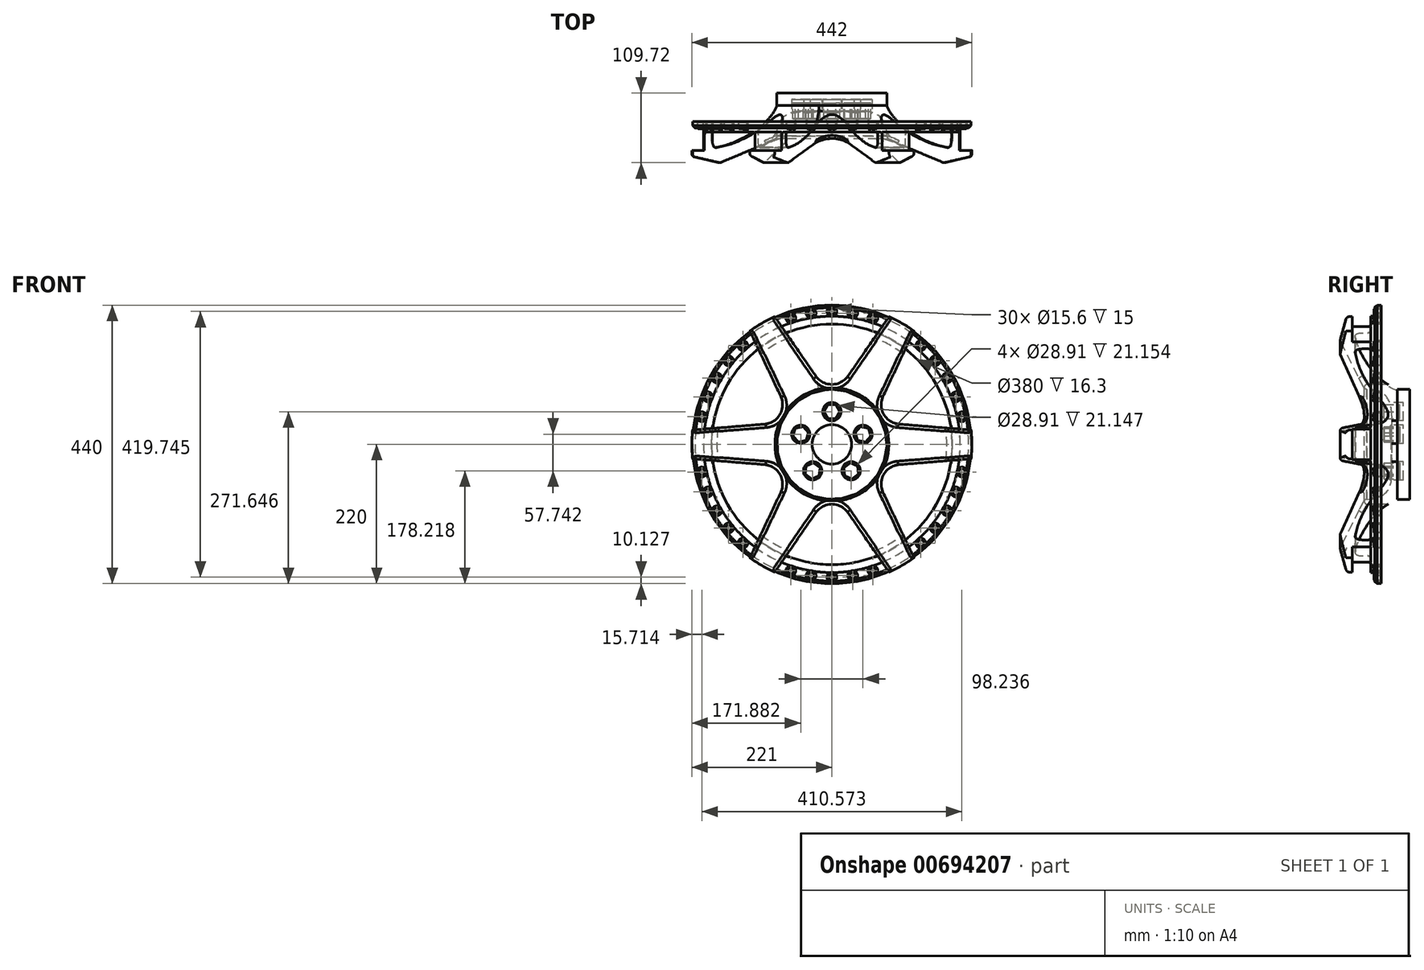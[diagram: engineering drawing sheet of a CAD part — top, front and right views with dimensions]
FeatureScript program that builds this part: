
annotation { "Feature Type Name" : "Feature", "Feature Type Description" : "" }
export const myFeature = defineFeature(function(context is Context, id is Id, definition is map)
    precondition{}
    {
        {
            var Q0;
            Q0=qCreatedBy(makeId("Front.planeOp"),FACE);
            var sketch = newSketch(context, id + "F0", { "sketchPlane" : qUnion([Q0])});
            skLineSegment(sketch, "E0", {"start": v(-376.44, 221) * mm, "end": v(379.77, 221) * mm, "construction": true});
            skLineSegment(sketch, "E1", {"start": v(-377.46, 0) * mm, "end": v(367.57, 0) * mm, "construction": true});
            skLineSegment(sketch, "E2", {"start": v(0, 375.13) * mm, "end": v(0, -409.58) * mm, "construction": true});
            skLineSegment(sketch, "E3", {"start": v(-369.36, 188.3) * mm, "end": v(384.11, 188.3) * mm, "construction": true});
            skLineSegment(sketch, "E4", {"start": v(-370.28, 96.42) * mm, "end": v(351.95, 96.42) * mm, "construction": true});
            skSolve(sketch);
        }
        {
            var Q0;
            Q0=qCreatedBy(makeId("Right.planeOp"),FACE);
            var sketch = newSketch(context, id + "F1", { "sketchPlane" : qUnion([Q0])});
            skLineSegment(sketch, "E5", {"start": v(-189.06, 0) * mm, "end": v(214.1, 0) * mm, "construction": true});
            skLineSegment(sketch, "E6", {"start": v(-201.77, 221) * mm, "end": v(212.06, 221) * mm, "construction": true});
            skLineSegment(sketch, "E7", {"start": v(-20.76, 221) * mm, "end": v(-30.79, 177.87) * mm});
            skLineSegment(sketch, "E8", {"start": v(8.3, 86.81) * mm, "end": v(8.3, 0) * mm});
            skLineSegment(sketch, "E9", {"start": v(8.3, 0) * mm, "end": v(79.17, 0) * mm});
            skLineSegment(sketch, "E10", {"start": v(79.17, 0) * mm, "end": v(79.17, 86.81) * mm});
            skLineSegment(sketch, "E11", {"start": v(79.17, 86.81) * mm, "end": v(59.77, 86.81) * mm});
            skFitSpline(sketch, "E12", {"points": [v(59.77, 86.81) * mm, v(-6.25, 181.47) * mm], "startDerivative": vector(-82.57, 26.6) * mm, "endDerivative": vector(-18.74, 115.71) * mm});
            skLineSegment(sketch, "E13", {"start": v(-20.76, 221) * mm, "end": v(-11.33, 221) * mm});
            skLineSegment(sketch, "E14", {"start": v(-11.33, 221) * mm, "end": v(-11.33, 202.63) * mm});
            skLineSegment(sketch, "E15", {"start": v(-11.33, 202.63) * mm, "end": v(19.19, 202.63) * mm});
            skLineSegment(sketch, "E16", {"start": v(19.19, 202.63) * mm, "end": v(19.19, 190.64) * mm});
            skFitSpline(sketch, "E17", {"points": [v(19.19, 190.64) * mm, v(-6.25, 181.47) * mm], "startDerivative": vector(-49.6, -1.13) * mm, "endDerivative": vector(9.02, -31.56) * mm});
            skLineSegment(sketch, "E18", {"start": v(-30.79, 177.87) * mm, "end": v(8.3, 86.81) * mm});
            skSolve(sketch);
        }
        {
            var Q0;
            Q0 = qSketchRegion(id + "F1", true);
            var Q1;
            Q1=sQuery(id+"F1.wireOp",EDGE,"E5");
            revolve(context, id + "F2", {"entities" : qUnion([Q0]), "axis" : qUnion([Q1]), "revolveType" : RevolveType.FULL});
        }
        {
            var Q0;
            Q0=qCreatedBy(makeId("Front.planeOp"),FACE);
            var sketch = newSketch(context, id + "F3", { "sketchPlane" : qUnion([Q0])});
            skLineSegment(sketch, "E19", {"start": v(0, 306.65) * mm, "end": v(0, -154.44) * mm, "construction": true});
            skLineSegment(sketch, "E20", {"start": v(-91.12, 202.94) * mm, "end": v(-25.47, 108.01) * mm});
            skLineSegment(sketch, "E21.MirrorCS", {"start": v(91.12, 202.94) * mm, "end": v(25.47, 108.01) * mm});
            skArc(sketch, "E22", {"start": v(-91.12, 202.94) * mm, "mid": v(0, 222.46) * mm, "end": v(91.12, 202.94) * mm});
            skArc(sketch, "E23", {"start": v(-25.47, 108.01) * mm, "mid": v(0, 94.66) * mm, "end": v(25.47, 108.01) * mm});
            skLineSegment(sketch, "E24.1.0", {"start": v(-130.2, 180.39) * mm, "end": v(-80.8, 76.06) * mm});
            skArc(sketch, "E24.1.1", {"start": v(-106.28, 31.95) * mm, "mid": v(-81.98, 47.33) * mm, "end": v(-80.8, 76.06) * mm});
            skLineSegment(sketch, "E24.1.2", {"start": v(-221.32, 22.56) * mm, "end": v(-106.28, 31.95) * mm});
            skArc(sketch, "E24.1.3", {"start": v(-221.32, 22.56) * mm, "mid": v(-192.66, 111.23) * mm, "end": v(-130.2, 180.39) * mm});
            skLineSegment(sketch, "E24.2.0", {"start": v(-221.32, -22.56) * mm, "end": v(-106.28, -31.95) * mm});
            skArc(sketch, "E24.2.1", {"start": v(-80.8, -76.06) * mm, "mid": v(-81.98, -47.33) * mm, "end": v(-106.28, -31.95) * mm});
            skLineSegment(sketch, "E24.2.2", {"start": v(-130.2, -180.39) * mm, "end": v(-80.8, -76.06) * mm});
            skArc(sketch, "E24.2.3", {"start": v(-130.2, -180.39) * mm, "mid": v(-192.66, -111.23) * mm, "end": v(-221.32, -22.56) * mm});
            skLineSegment(sketch, "E24.3.0", {"start": v(-91.12, -202.94) * mm, "end": v(-25.47, -108.01) * mm});
            skArc(sketch, "E24.3.1", {"start": v(25.47, -108.01) * mm, "mid": v(0, -94.66) * mm, "end": v(-25.47, -108.01) * mm});
            skLineSegment(sketch, "E24.3.2", {"start": v(91.12, -202.94) * mm, "end": v(25.47, -108.01) * mm});
            skArc(sketch, "E24.3.3", {"start": v(91.12, -202.94) * mm, "mid": v(0, -222.46) * mm, "end": v(-91.12, -202.94) * mm});
            skLineSegment(sketch, "E24.4.0", {"start": v(130.2, -180.39) * mm, "end": v(80.8, -76.06) * mm});
            skArc(sketch, "E24.4.1", {"start": v(106.28, -31.95) * mm, "mid": v(81.98, -47.33) * mm, "end": v(80.8, -76.06) * mm});
            skLineSegment(sketch, "E24.4.2", {"start": v(221.32, -22.56) * mm, "end": v(106.28, -31.95) * mm});
            skArc(sketch, "E24.4.3", {"start": v(221.32, -22.56) * mm, "mid": v(192.66, -111.23) * mm, "end": v(130.2, -180.39) * mm});
            skLineSegment(sketch, "E24.5.0", {"start": v(221.32, 22.56) * mm, "end": v(106.28, 31.95) * mm});
            skArc(sketch, "E24.5.1", {"start": v(80.8, 76.06) * mm, "mid": v(81.98, 47.33) * mm, "end": v(106.28, 31.95) * mm});
            skLineSegment(sketch, "E24.5.2", {"start": v(130.2, 180.39) * mm, "end": v(80.8, 76.06) * mm});
            skArc(sketch, "E24.5.3", {"start": v(130.2, 180.39) * mm, "mid": v(192.66, 111.23) * mm, "end": v(221.32, 22.56) * mm});
            skSolve(sketch);
        }
        {
            var Q0;
            Q0 = qSketchRegion(id + "F3", true);
            extrude(context, id + "F4", {"entities" : qUnion([Q0]), "operationType" : NewBodyOperationType.REMOVE, "oppositeDirection" : true, "depth" : 214 * mm, "offsetDistance" : 25 * mm, "symmetric" : true});
        }
        {
            var Q0;
            Q0=qCreatedBy(makeId("Front.planeOp"),FACE);
            var sketch = newSketch(context, id + "F5", { "sketchPlane" : qUnion([Q0])});
            skCircle(sketch, "E25.0", {"center": v(0, 0) * mm, "radius": 86.81 * mm});
            skSolve(sketch);
        }
        {
            var Q0;
            Q0 = qSketchRegion(id + "F5", true);
            extrude(context, id + "F6", {"entities" : qUnion([Q0]), "operationType" : NewBodyOperationType.REMOVE, "oppositeDirection" : true, "depth" : 51 * mm, "offsetDistance" : 25 * mm});
        }
        {
            var Q0;
            Q0=makeQuery(id+"F6.boolean.opBoolean","COPY",EDGE,{"derivedFrom":makeQuery(id+"F6.opExtrude","CAP_EDGE",EDGE,{"disambiguationData":[OSD([sQuery(id+"F5.wireOp",EDGE,"E25.0")])],"isStart":false})});
            fillet(context, id + "F7", {"entities" : qUnion([Q0]), "radius" : 40 * mm, "tangentPropagation" : true, "rho" : 0.5, "crossSection" : FilletCrossSection.CONIC, "allowEdgeOverflow" : false});
        }
        {
            var Q0;
            Q0=makeQuery(id+"F2.opRevolve","SWEPT_FACE",FACE,{"disambiguationData":[OSD([sQuery(id+"F1.wireOp",EDGE,"E18")])]});
            var Q1;
            Q1=makeQuery(id+"F4.boolean.opBoolean","SPLIT",FACE,{"disambiguationData":[TD([makeQuery(id+"F4.opExtrude","SWEPT_FACE",FACE,{"disambiguationData":[OSD([sQuery(id+"F3.wireOp",EDGE,"E24.1.2")])]})])],"derivedFrom":makeQuery(id+"F2.opRevolve","SWEPT_FACE",FACE,{"disambiguationData":[OSD([sQuery(id+"F1.wireOp",EDGE,"E7")])]})});
            var Q2;
            Q2=makeQuery(id+"F4.boolean.opBoolean","SPLIT",FACE,{"disambiguationData":[TD([makeQuery(id+"F4.opExtrude","SWEPT_FACE",FACE,{"disambiguationData":[OSD([sQuery(id+"F3.wireOp",EDGE,"E24.2.2")])]})])],"derivedFrom":makeQuery(id+"F2.opRevolve","SWEPT_FACE",FACE,{"disambiguationData":[OSD([sQuery(id+"F1.wireOp",EDGE,"E7")])]})});
            var Q3;
            Q3=makeQuery(id+"F4.boolean.opBoolean","SPLIT",FACE,{"disambiguationData":[TD([makeQuery(id+"F4.opExtrude","SWEPT_FACE",FACE,{"disambiguationData":[OSD([sQuery(id+"F3.wireOp",EDGE,"E24.3.2")])]})])],"derivedFrom":makeQuery(id+"F2.opRevolve","SWEPT_FACE",FACE,{"disambiguationData":[OSD([sQuery(id+"F1.wireOp",EDGE,"E7")])]})});
            var Q4;
            Q4=makeQuery(id+"F4.boolean.opBoolean","SPLIT",FACE,{"disambiguationData":[TD([makeQuery(id+"F4.opExtrude","SWEPT_FACE",FACE,{"disambiguationData":[OSD([sQuery(id+"F3.wireOp",EDGE,"E24.4.2")])]})])],"derivedFrom":makeQuery(id+"F2.opRevolve","SWEPT_FACE",FACE,{"disambiguationData":[OSD([sQuery(id+"F1.wireOp",EDGE,"E7")])]})});
            var Q5;
            Q5=makeQuery(id+"F4.boolean.opBoolean","SPLIT",FACE,{"disambiguationData":[TD([makeQuery(id+"F4.opExtrude","SWEPT_FACE",FACE,{"disambiguationData":[OSD([sQuery(id+"F3.wireOp",EDGE,"E21.MirrorCS")])]})])],"derivedFrom":makeQuery(id+"F2.opRevolve","SWEPT_FACE",FACE,{"disambiguationData":[OSD([sQuery(id+"F1.wireOp",EDGE,"E7")])]})});
            var Q6;
            Q6=makeQuery(id+"F4.boolean.opBoolean","SPLIT",FACE,{"disambiguationData":[TD([makeQuery(id+"F4.opExtrude","SWEPT_FACE",FACE,{"disambiguationData":[OSD([sQuery(id+"F3.wireOp",EDGE,"E20")])]})])],"derivedFrom":makeQuery(id+"F2.opRevolve","SWEPT_FACE",FACE,{"disambiguationData":[OSD([sQuery(id+"F1.wireOp",EDGE,"E7")])]})});
            fillet(context, id + "F8", {"entities" : qUnion([Q0, Q1, Q2, Q3, Q4, Q5, Q6]), "radius" : 5 * mm, "tangentPropagation" : true, "allowEdgeOverflow" : false});
        }
        {
            var Q0;
            Q0=qCreatedBy(makeId("Front.planeOp"),FACE);
            cPlane(context, id + "F9", {"entities" : qUnion([Q0]), "cplaneType" : CPlaneType.OFFSET, "offset" : 18 * mm, "oppositeDirection" : true, "width" : 150 * mm, "height" : 150 * mm});
        }
        {
            var Q0;
            Q0=qCreatedBy(id+"F9.planeOp",FACE);
            var sketch = newSketch(context, id + "F10", { "sketchPlane" : qUnion([Q0])});
            skCircle(sketch, "E26", {"center": v(0, 0) * mm, "radius": 220 * mm});
            skCircle(sketch, "E27", {"center": v(0, 0) * mm, "radius": 190 * mm});
            skSolve(sketch);
        }
        {
            var Q0;
            Q0 = qSketchRegion(id + "F10", true);
            extrude(context, id + "F11", {"entities" : qUnion([Q0]), "operationType" : NewBodyOperationType.ADD, "oppositeDirection" : true, "depth" : 16.3 * mm, "offsetDistance" : 25 * mm});
        }
        {
            var Q0;
            Q0=makeQuery(id+"F11.opExtrude","CAP_FACE",FACE,{"disambiguationData":[OSD([sQuery(id+"F10.wireOp",EDGE,"E26"),sQuery(id+"F10.wireOp",EDGE,"E27")])],"isStart":true});
            var sketch = newSketch(context, id + "F12", { "sketchPlane" : qUnion([Q0])});
            skCircle(sketch, "E28", {"center": v(0, 0) * mm, "radius": 235.3 * mm});
            skCircle(sketch, "E29", {"center": v(0, 0) * mm, "radius": 202.5 * mm});
            skSolve(sketch);
        }
        {
            var Q0;
            Q0 = qSketchRegion(id + "F12", true);
            extrude(context, id + "F13", {"entities" : qUnion([Q0]), "operationType" : NewBodyOperationType.REMOVE, "oppositeDirection" : true, "depth" : 6 * mm, "offsetDistance" : 25 * mm});
        }
        {
            var Q0;
            Q0=makeQuery(id+"F13.boolean.opBoolean","COPY",EDGE,{"derivedFrom":makeQuery(id+"F13.opExtrude","CAP_EDGE",EDGE,{"disambiguationData":[OSD([sQuery(id+"F12.wireOp",EDGE,"E29")])],"isStart":false})});
            fillet(context, id + "F14", {"entities" : qUnion([Q0]), "radius" : 5 * mm, "tangentPropagation" : true, "allowEdgeOverflow" : false});
        }
        {
            var Q0;
            {var subQ0=makeQuery(id+"F4.boolean.opBoolean","COPY",FACE,{"derivedFrom":makeQuery(id+"F4.opExtrude","SWEPT_FACE",FACE,{"disambiguationData":[OSD([sQuery(id+"F3.wireOp",EDGE,"E24.1.0")])]})});var subQ1=makeQuery(id+"F11.opExtrude","CAP_FACE",FACE,{"disambiguationData":[OSD([sQuery(id+"F10.wireOp",EDGE,"E26"),sQuery(id+"F10.wireOp",EDGE,"E27")])],"isStart":true});Q0=makeQuery(id+"F13.boolean.opBoolean","SPLIT",EDGE,{"disambiguationData":[topologyDisambiguationEdgeConnected([subQ1])],"derivedFrom":makeQuery(id+"F11.boolean.opBoolean","INTERSECT",EDGE,{"derivedFrom":[subQ0,subQ1]})});}
            var Q1;
            {var subQ0=makeQuery(id+"F4.boolean.opBoolean","COPY",FACE,{"derivedFrom":makeQuery(id+"F4.opExtrude","SWEPT_FACE",FACE,{"disambiguationData":[OSD([sQuery(id+"F3.wireOp",EDGE,"E20")])]})});var subQ1=makeQuery(id+"F11.opExtrude","CAP_FACE",FACE,{"disambiguationData":[OSD([sQuery(id+"F10.wireOp",EDGE,"E26"),sQuery(id+"F10.wireOp",EDGE,"E27")])],"isStart":true});Q1=makeQuery(id+"F13.boolean.opBoolean","SPLIT",EDGE,{"disambiguationData":[topologyDisambiguationEdgeConnected([subQ1])],"derivedFrom":makeQuery(id+"F11.boolean.opBoolean","INTERSECT",EDGE,{"derivedFrom":[subQ0,subQ1]})});}
            var Q2;
            {var subQ0=makeQuery(id+"F4.boolean.opBoolean","COPY",FACE,{"derivedFrom":makeQuery(id+"F4.opExtrude","SWEPT_FACE",FACE,{"disambiguationData":[OSD([sQuery(id+"F3.wireOp",EDGE,"E21.MirrorCS")])]})});var subQ1=makeQuery(id+"F11.opExtrude","CAP_FACE",FACE,{"disambiguationData":[OSD([sQuery(id+"F10.wireOp",EDGE,"E26"),sQuery(id+"F10.wireOp",EDGE,"E27")])],"isStart":true});Q2=makeQuery(id+"F13.boolean.opBoolean","SPLIT",EDGE,{"disambiguationData":[topologyDisambiguationEdgeConnected([subQ1])],"derivedFrom":makeQuery(id+"F11.boolean.opBoolean","INTERSECT",EDGE,{"derivedFrom":[subQ0,subQ1]})});}
            var Q3;
            {var subQ0=makeQuery(id+"F4.boolean.opBoolean","COPY",FACE,{"derivedFrom":makeQuery(id+"F4.opExtrude","SWEPT_FACE",FACE,{"disambiguationData":[OSD([sQuery(id+"F3.wireOp",EDGE,"E24.5.2")])]})});var subQ1=makeQuery(id+"F11.opExtrude","CAP_FACE",FACE,{"disambiguationData":[OSD([sQuery(id+"F10.wireOp",EDGE,"E26"),sQuery(id+"F10.wireOp",EDGE,"E27")])],"isStart":true});Q3=makeQuery(id+"F13.boolean.opBoolean","SPLIT",EDGE,{"disambiguationData":[topologyDisambiguationEdgeConnected([subQ1])],"derivedFrom":makeQuery(id+"F11.boolean.opBoolean","INTERSECT",EDGE,{"derivedFrom":[subQ0,subQ1]})});}
            var Q4;
            {var subQ0=makeQuery(id+"F4.boolean.opBoolean","COPY",FACE,{"derivedFrom":makeQuery(id+"F4.opExtrude","SWEPT_FACE",FACE,{"disambiguationData":[OSD([sQuery(id+"F3.wireOp",EDGE,"E24.4.2")])]})});var subQ1=makeQuery(id+"F11.opExtrude","CAP_FACE",FACE,{"disambiguationData":[OSD([sQuery(id+"F10.wireOp",EDGE,"E26"),sQuery(id+"F10.wireOp",EDGE,"E27")])],"isStart":true});Q4=makeQuery(id+"F13.boolean.opBoolean","SPLIT",EDGE,{"disambiguationData":[topologyDisambiguationEdgeConnected([subQ1])],"derivedFrom":makeQuery(id+"F11.boolean.opBoolean","INTERSECT",EDGE,{"derivedFrom":[subQ0,subQ1]})});}
            var Q5;
            {var subQ0=makeQuery(id+"F4.boolean.opBoolean","COPY",FACE,{"derivedFrom":makeQuery(id+"F4.opExtrude","SWEPT_FACE",FACE,{"disambiguationData":[OSD([sQuery(id+"F3.wireOp",EDGE,"E24.5.0")])]})});var subQ1=makeQuery(id+"F11.opExtrude","CAP_FACE",FACE,{"disambiguationData":[OSD([sQuery(id+"F10.wireOp",EDGE,"E26"),sQuery(id+"F10.wireOp",EDGE,"E27")])],"isStart":true});Q5=makeQuery(id+"F13.boolean.opBoolean","SPLIT",EDGE,{"disambiguationData":[topologyDisambiguationEdgeConnected([subQ1])],"derivedFrom":makeQuery(id+"F11.boolean.opBoolean","INTERSECT",EDGE,{"derivedFrom":[subQ0,subQ1]})});}
            var Q6;
            {var subQ0=makeQuery(id+"F4.boolean.opBoolean","COPY",FACE,{"derivedFrom":makeQuery(id+"F4.opExtrude","SWEPT_FACE",FACE,{"disambiguationData":[OSD([sQuery(id+"F3.wireOp",EDGE,"E24.4.0")])]})});var subQ1=makeQuery(id+"F11.opExtrude","CAP_FACE",FACE,{"disambiguationData":[OSD([sQuery(id+"F10.wireOp",EDGE,"E26"),sQuery(id+"F10.wireOp",EDGE,"E27")])],"isStart":true});Q6=makeQuery(id+"F13.boolean.opBoolean","SPLIT",EDGE,{"disambiguationData":[topologyDisambiguationEdgeConnected([subQ1])],"derivedFrom":makeQuery(id+"F11.boolean.opBoolean","INTERSECT",EDGE,{"derivedFrom":[subQ0,subQ1]})});}
            var Q7;
            {var subQ0=makeQuery(id+"F4.boolean.opBoolean","COPY",FACE,{"derivedFrom":makeQuery(id+"F4.opExtrude","SWEPT_FACE",FACE,{"disambiguationData":[OSD([sQuery(id+"F3.wireOp",EDGE,"E24.3.2")])]})});var subQ1=makeQuery(id+"F11.opExtrude","CAP_FACE",FACE,{"disambiguationData":[OSD([sQuery(id+"F10.wireOp",EDGE,"E26"),sQuery(id+"F10.wireOp",EDGE,"E27")])],"isStart":true});Q7=makeQuery(id+"F13.boolean.opBoolean","SPLIT",EDGE,{"disambiguationData":[topologyDisambiguationEdgeConnected([subQ1])],"derivedFrom":makeQuery(id+"F11.boolean.opBoolean","INTERSECT",EDGE,{"derivedFrom":[subQ0,subQ1]})});}
            var Q8;
            {var subQ0=makeQuery(id+"F4.boolean.opBoolean","COPY",FACE,{"derivedFrom":makeQuery(id+"F4.opExtrude","SWEPT_FACE",FACE,{"disambiguationData":[OSD([sQuery(id+"F3.wireOp",EDGE,"E24.2.2")])]})});var subQ1=makeQuery(id+"F11.opExtrude","CAP_FACE",FACE,{"disambiguationData":[OSD([sQuery(id+"F10.wireOp",EDGE,"E26"),sQuery(id+"F10.wireOp",EDGE,"E27")])],"isStart":true});Q8=makeQuery(id+"F13.boolean.opBoolean","SPLIT",EDGE,{"disambiguationData":[topologyDisambiguationEdgeConnected([subQ1])],"derivedFrom":makeQuery(id+"F11.boolean.opBoolean","INTERSECT",EDGE,{"derivedFrom":[subQ0,subQ1]})});}
            var Q9;
            {var subQ0=makeQuery(id+"F4.boolean.opBoolean","COPY",FACE,{"derivedFrom":makeQuery(id+"F4.opExtrude","SWEPT_FACE",FACE,{"disambiguationData":[OSD([sQuery(id+"F3.wireOp",EDGE,"E24.3.0")])]})});var subQ1=makeQuery(id+"F11.opExtrude","CAP_FACE",FACE,{"disambiguationData":[OSD([sQuery(id+"F10.wireOp",EDGE,"E26"),sQuery(id+"F10.wireOp",EDGE,"E27")])],"isStart":true});Q9=makeQuery(id+"F13.boolean.opBoolean","SPLIT",EDGE,{"disambiguationData":[topologyDisambiguationEdgeConnected([subQ1])],"derivedFrom":makeQuery(id+"F11.boolean.opBoolean","INTERSECT",EDGE,{"derivedFrom":[subQ0,subQ1]})});}
            var Q10;
            {var subQ0=makeQuery(id+"F4.boolean.opBoolean","COPY",FACE,{"derivedFrom":makeQuery(id+"F4.opExtrude","SWEPT_FACE",FACE,{"disambiguationData":[OSD([sQuery(id+"F3.wireOp",EDGE,"E24.1.2")])]})});var subQ1=makeQuery(id+"F11.opExtrude","CAP_FACE",FACE,{"disambiguationData":[OSD([sQuery(id+"F10.wireOp",EDGE,"E26"),sQuery(id+"F10.wireOp",EDGE,"E27")])],"isStart":true});Q10=makeQuery(id+"F13.boolean.opBoolean","SPLIT",EDGE,{"disambiguationData":[topologyDisambiguationEdgeConnected([subQ1])],"derivedFrom":makeQuery(id+"F11.boolean.opBoolean","INTERSECT",EDGE,{"derivedFrom":[subQ0,subQ1]})});}
            var Q11;
            {var subQ0=makeQuery(id+"F4.boolean.opBoolean","COPY",FACE,{"derivedFrom":makeQuery(id+"F4.opExtrude","SWEPT_FACE",FACE,{"disambiguationData":[OSD([sQuery(id+"F3.wireOp",EDGE,"E24.2.0")])]})});var subQ1=makeQuery(id+"F11.opExtrude","CAP_FACE",FACE,{"disambiguationData":[OSD([sQuery(id+"F10.wireOp",EDGE,"E26"),sQuery(id+"F10.wireOp",EDGE,"E27")])],"isStart":true});Q11=makeQuery(id+"F13.boolean.opBoolean","SPLIT",EDGE,{"disambiguationData":[topologyDisambiguationEdgeConnected([subQ1])],"derivedFrom":makeQuery(id+"F11.boolean.opBoolean","INTERSECT",EDGE,{"derivedFrom":[subQ0,subQ1]})});}
            fillet(context, id + "F15", {"entities" : qUnion([Q0, Q1, Q2, Q3, Q4, Q5, Q6, Q7, Q8, Q9, Q10, Q11]), "radius" : 5 * mm, "tangentPropagation" : true, "allowEdgeOverflow" : false});
        }
        {
            var Q0;
            Q0=makeQuery(id+"F11.opExtrude","CAP_FACE",FACE,{"disambiguationData":[OSD([sQuery(id+"F10.wireOp",EDGE,"E26"),sQuery(id+"F10.wireOp",EDGE,"E27")])],"isStart":true});
            var sketch = newSketch(context, id + "F16", { "sketchPlane" : qUnion([Q0])});
            skCircle(sketch, "E30", {"center": v(0, 209.87) * mm, "radius": 7.8 * mm});
            skLineSegment(sketch, "E31", {"start": v(0, 0) * mm, "end": v(-146.93, 254.49) * mm, "construction": true});
            skLineSegment(sketch, "E32", {"start": v(0, 0) * mm, "end": v(-77.22, 237.67) * mm, "construction": true});
            skCircle(sketch, "E33", {"center": v(0, 0) * mm, "radius": 209.87 * mm, "construction": true});
            skLineSegment(sketch, "E34", {"start": v(0, 0) * mm, "end": v(-39.2, 247.52) * mm, "construction": true});
            skCircle(sketch, "E35", {"center": v(-32.83, 207.29) * mm, "radius": 7.8 * mm});
            skCircle(sketch, "E36", {"center": v(-64.85, 199.6) * mm, "radius": 7.8 * mm});
            skCircle(sketch, "E37.MirrorC", {"center": v(32.83, 207.29) * mm, "radius": 7.8 * mm});
            skCircle(sketch, "E38.MirrorC", {"center": v(64.85, 199.6) * mm, "radius": 7.8 * mm});
            skCircle(sketch, "E39.1.0", {"center": v(-205.29, 43.63) * mm, "radius": 7.8 * mm});
            skCircle(sketch, "E39.1.1", {"center": v(-195.93, 75.21) * mm, "radius": 7.8 * mm});
            skCircle(sketch, "E39.1.2", {"center": v(-181.76, 104.94) * mm, "radius": 7.8 * mm});
            skCircle(sketch, "E39.1.3", {"center": v(-163.1, 132.08) * mm, "radius": 7.8 * mm});
            skCircle(sketch, "E39.1.4", {"center": v(-140.43, 155.97) * mm, "radius": 7.8 * mm});
            skCircle(sketch, "E39.2.0", {"center": v(-140.43, -155.97) * mm, "radius": 7.8 * mm});
            skCircle(sketch, "E39.2.1", {"center": v(-163.1, -132.08) * mm, "radius": 7.8 * mm});
            skCircle(sketch, "E39.2.2", {"center": v(-181.76, -104.94) * mm, "radius": 7.8 * mm});
            skCircle(sketch, "E39.2.3", {"center": v(-195.93, -75.21) * mm, "radius": 7.8 * mm});
            skCircle(sketch, "E39.2.4", {"center": v(-205.29, -43.63) * mm, "radius": 7.8 * mm});
            skCircle(sketch, "E39.3.0", {"center": v(64.85, -199.6) * mm, "radius": 7.8 * mm});
            skCircle(sketch, "E39.3.1", {"center": v(32.83, -207.29) * mm, "radius": 7.8 * mm});
            skCircle(sketch, "E39.3.2", {"center": v(0, -209.87) * mm, "radius": 7.8 * mm});
            skCircle(sketch, "E39.3.3", {"center": v(-32.83, -207.29) * mm, "radius": 7.8 * mm});
            skCircle(sketch, "E39.3.4", {"center": v(-64.85, -199.6) * mm, "radius": 7.8 * mm});
            skCircle(sketch, "E39.4.0", {"center": v(205.29, -43.63) * mm, "radius": 7.8 * mm});
            skCircle(sketch, "E39.4.1", {"center": v(195.93, -75.21) * mm, "radius": 7.8 * mm});
            skCircle(sketch, "E39.4.2", {"center": v(181.76, -104.94) * mm, "radius": 7.8 * mm});
            skCircle(sketch, "E39.4.3", {"center": v(163.1, -132.08) * mm, "radius": 7.8 * mm});
            skCircle(sketch, "E39.4.4", {"center": v(140.43, -155.97) * mm, "radius": 7.8 * mm});
            skCircle(sketch, "E39.5.0", {"center": v(140.43, 155.97) * mm, "radius": 7.8 * mm});
            skCircle(sketch, "E39.5.1", {"center": v(163.1, 132.08) * mm, "radius": 7.8 * mm});
            skCircle(sketch, "E39.5.2", {"center": v(181.76, 104.94) * mm, "radius": 7.8 * mm});
            skCircle(sketch, "E39.5.3", {"center": v(195.93, 75.21) * mm, "radius": 7.8 * mm});
            skCircle(sketch, "E39.5.4", {"center": v(205.29, 43.63) * mm, "radius": 7.8 * mm});
            skSolve(sketch);
        }
        {
            var Q0;
            Q0 = qSketchRegion(id + "F16", true);
            extrude(context, id + "F17", {"entities" : qUnion([Q0]), "operationType" : NewBodyOperationType.REMOVE, "oppositeDirection" : true, "depth" : 15 * mm, "offsetDistance" : 25 * mm});
        }
        {
            var Q0;
            Q0=makeQuery(id+"F6.boolean.opBoolean","COPY",FACE,{"derivedFrom":makeQuery(id+"F6.opExtrude","CAP_FACE",FACE,{"disambiguationData":[OSD([sQuery(id+"F5.wireOp",EDGE,"E25.0")])],"isStart":false})});
            var sketch = newSketch(context, id + "F18", { "sketchPlane" : qUnion([Q0])});
            skCircle(sketch, "E40", {"center": v(0, 0) * mm, "radius": 31 * mm});
            skSolve(sketch);
        }
        {
            var Q0;
            Q0 = qSketchRegion(id + "F18", true);
            extrude(context, id + "F19", {"entities" : qUnion([Q0]), "operationType" : NewBodyOperationType.ADD, "depth" : 0.9 * mm, "offsetDistance" : 25 * mm});
        }
        {
            var Q0;
            Q0=makeQuery(id+"F6.boolean.opBoolean","COPY",FACE,{"derivedFrom":makeQuery(id+"F6.opExtrude","CAP_FACE",FACE,{"disambiguationData":[OSD([sQuery(id+"F5.wireOp",EDGE,"E25.0")])],"isStart":false})});
            var sketch = newSketch(context, id + "F20", { "sketchPlane" : qUnion([Q0])});
            skCircle(sketch, "E41", {"center": v(0, 51.65) * mm, "radius": 14.46 * mm});
            skCircle(sketch, "E42.1.0", {"center": v(-49.12, 15.96) * mm, "radius": 14.46 * mm});
            skCircle(sketch, "E42.2.0", {"center": v(-30.36, -41.78) * mm, "radius": 14.46 * mm});
            skCircle(sketch, "E42.3.0", {"center": v(30.36, -41.78) * mm, "radius": 14.46 * mm});
            skCircle(sketch, "E42.4.0", {"center": v(49.12, 15.96) * mm, "radius": 14.46 * mm});
            skPoint(sketch, "E42.center", {"position": v(0, 0) * mm});
            skSolve(sketch);
        }
        {
            var Q0;
            Q0 = qSketchRegion(id + "F20", true);
            extrude(context, id + "F21", {"entities" : qUnion([Q0]), "operationType" : NewBodyOperationType.REMOVE, "oppositeDirection" : true, "depth" : 36 * mm, "offsetDistance" : 25 * mm, "symmetric" : true});
        }
        {
            var Q0;
            Q0=makeQuery(id+"F6.boolean.opBoolean","COPY",FACE,{"derivedFrom":makeQuery(id+"F6.opExtrude","CAP_FACE",FACE,{"disambiguationData":[OSD([sQuery(id+"F5.wireOp",EDGE,"E25.0")])],"isStart":false})});
            var sketch = newSketch(context, id + "F22", { "sketchPlane" : qUnion([Q0])});
            skArc(sketch, "E43.0", {"start": v(12.85, 45.01) * mm, "mid": v(0, 66.1) * mm, "end": v(-12.85, 45.01) * mm});
            skCircle(sketch, "E44.cCircle", {"center": v(0, 51.65) * mm, "radius": 11 * mm, "construction": true});
            skLineSegment(sketch, "E44.0", {"start": v(-6.35, 62.65) * mm, "end": v(6.35, 62.65) * mm});
            skLineSegment(sketch, "E44.1", {"start": v(6.35, 62.65) * mm, "end": v(12.7, 51.65) * mm});
            skLineSegment(sketch, "E44.2", {"start": v(12.7, 51.65) * mm, "end": v(6.35, 40.65) * mm});
            skLineSegment(sketch, "E44.3", {"start": v(6.35, 40.65) * mm, "end": v(-6.35, 40.65) * mm});
            skLineSegment(sketch, "E44.4", {"start": v(-6.35, 40.65) * mm, "end": v(-12.7, 51.65) * mm});
            skLineSegment(sketch, "E44.5", {"start": v(-12.7, 51.65) * mm, "end": v(-6.35, 62.65) * mm});
            skPoint(sketch, "E44.0.midPoint", {"position": v(0, 62.65) * mm});
            skSolve(sketch);
        }
        {
            var Q0;
            Q0 = qSketchRegion(id + "F22", true);
            extrude(context, id + "F23", {"entities" : qUnion([Q0]), "depth" : 25 * mm, "offsetDistance" : 25 * mm, "symmetric" : true});
        }
        {
            var Q0;
            Q0=makeQuery(id+"F23.opExtrude","CAP_FACE",FACE,{"disambiguationData":[OSD([sQuery(id+"F22.wireOp",EDGE,"E44.0"),sQuery(id+"F22.wireOp",EDGE,"E44.1"),sQuery(id+"F22.wireOp",EDGE,"E44.2"),sQuery(id+"F22.wireOp",EDGE,"E44.3"),sQuery(id+"F22.wireOp",EDGE,"E44.4"),sQuery(id+"F22.wireOp",EDGE,"E44.5")])],"isStart":false});
            var sketch = newSketch(context, id + "F24", { "sketchPlane" : qUnion([Q0])});
            skCircle(sketch, "E45", {"center": v(0, 51.65) * mm, "radius": 9.3 * mm});
            skSolve(sketch);
        }
        {
            var Q0;
            Q0 = qSketchRegion(id + "F24", true);
            extrude(context, id + "F25", {"entities" : qUnion([Q0]), "operationType" : NewBodyOperationType.ADD, "depth" : 4.4 * mm, "offsetDistance" : 25 * mm});
        }
        {
            var Q0;
            Q0=makeQuery(id+"F25.opExtrude","CAP_EDGE",EDGE,{"disambiguationData":[OSD([sQuery(id+"F24.wireOp",EDGE,"E45")])],"isStart":false});
            fillet(context, id + "F26", {"entities" : qUnion([Q0]), "radius" : 5 * mm, "tangentPropagation" : true, "allowEdgeOverflow" : false});
        }
        {
            var Q0;
            Q0=makeQuery(id+"F23.opExtrude","CAP_FACE",FACE,{"disambiguationData":[OSD([sQuery(id+"F22.wireOp",EDGE,"E44.0"),sQuery(id+"F22.wireOp",EDGE,"E44.1"),sQuery(id+"F22.wireOp",EDGE,"E44.2"),sQuery(id+"F22.wireOp",EDGE,"E44.3"),sQuery(id+"F22.wireOp",EDGE,"E44.4"),sQuery(id+"F22.wireOp",EDGE,"E44.5")])],"isStart":false});
            fillet(context, id + "F27", {"entities" : qUnion([Q0]), "radius" : .5 * mm, "tangentPropagation" : true, "allowEdgeOverflow" : false});
        }
        {
            var Q0;
            Q0=makeQuery(id+"F23.opExtrude","SWEPT_BODY",BODY,{"disambiguationData":[OSD([sQuery(id+"F22.wireOp",EDGE,"E44.0"),sQuery(id+"F22.wireOp",EDGE,"E44.1"),sQuery(id+"F22.wireOp",EDGE,"E44.2"),sQuery(id+"F22.wireOp",EDGE,"E44.3"),sQuery(id+"F22.wireOp",EDGE,"E44.4"),sQuery(id+"F22.wireOp",EDGE,"E44.5")])]});
            var Q1;
            Q1=sQuery(id+"F1.wireOp",EDGE,"E5");
            circularPattern(context, id + "F28", {"entities" : qUnion([Q0]), "axis" : qUnion([Q1]), "angle" : 360 * degree, "instanceCount" : 5, "equalSpace" : true, "computeTransformsWithoutBuiltin" : true});
        }
        {
            var Q0;
            Q0=makeQuery(id+"F11.opExtrude","CAP_FACE",FACE,{"disambiguationData":[OSD([sQuery(id+"F10.wireOp",EDGE,"E26"),sQuery(id+"F10.wireOp",EDGE,"E27")])],"isStart":false});
            var sketch = newSketch(context, id + "F29", { "sketchPlane" : qUnion([Q0])});
            skCircle(sketch, "E46", {"center": v(0, 209.87) * mm, "radius": 6.5 * mm});
            skCircle(sketch, "E47", {"center": v(32.83, 207.29) * mm, "radius": 6.5 * mm});
            skCircle(sketch, "E48", {"center": v(64.85, 199.6) * mm, "radius": 6.5 * mm});
            skCircle(sketch, "E49", {"center": v(-32.83, 207.29) * mm, "radius": 6.5 * mm});
            skCircle(sketch, "E50", {"center": v(-64.85, 199.6) * mm, "radius": 6.5 * mm});
            skSolve(sketch);
        }
        {
            var Q0;
            Q0 = qSketchRegion(id + "F29", true);
            extrude(context, id + "F30", {"entities" : qUnion([Q0]), "oppositeDirection" : true, "depth" : 11.5 * mm, "offsetDistance" : 25 * mm});
        }
        {
            var Q0;
            Q0=makeQuery(id+"F13.boolean.opBoolean","INTERSECT",EDGE,{"derivedFrom":[makeQuery(id+"F11.opExtrude","SWEPT_FACE",FACE,{"disambiguationData":[OSD([sQuery(id+"F10.wireOp",EDGE,"E26")])]}),makeQuery(id+"F13.opExtrude","CAP_FACE",FACE,{"disambiguationData":[OSD([sQuery(id+"F12.wireOp",EDGE,"E28"),sQuery(id+"F12.wireOp",EDGE,"E29")])],"isStart":false})]});
            chamfer(context, id + "F31", {"entities" : qUnion([Q0]), "width" : 4 * mm, "tangentPropagation" : true});
        }
        {
            var Q0;
            Q0=makeQuery(id+"F30.opExtrude","CAP_FACE",FACE,{"disambiguationData":[OSD([sQuery(id+"F29.wireOp",EDGE,"E46")])],"isStart":false});
            var sketch = newSketch(context, id + "F32", { "sketchPlane" : qUnion([Q0])});
            skCircle(sketch, "E51.cCircle", {"center": v(0, 209.87) * mm, "radius": 4.63 * mm, "construction": true});
            skLineSegment(sketch, "E51.0", {"start": v(-2.67, 214.5) * mm, "end": v(2.67, 214.5) * mm});
            skLineSegment(sketch, "E51.1", {"start": v(2.67, 214.5) * mm, "end": v(5.35, 209.87) * mm});
            skLineSegment(sketch, "E51.2", {"start": v(5.35, 209.87) * mm, "end": v(2.67, 205.24) * mm});
            skLineSegment(sketch, "E51.3", {"start": v(2.67, 205.24) * mm, "end": v(-2.67, 205.24) * mm});
            skLineSegment(sketch, "E51.4", {"start": v(-2.67, 205.24) * mm, "end": v(-5.35, 209.87) * mm});
            skLineSegment(sketch, "E51.5", {"start": v(-5.35, 209.87) * mm, "end": v(-2.67, 214.5) * mm});
            skPoint(sketch, "E51.0.midPoint", {"position": v(0, 214.5) * mm});
            skCircle(sketch, "E52.0", {"center": v(-32.83, 207.29) * mm, "radius": 6.5 * mm, "construction": true});
            skCircle(sketch, "E53.cCircle", {"center": v(-32.83, 207.29) * mm, "radius": 4.66 * mm, "construction": true});
            skLineSegment(sketch, "E53.0", {"start": v(-35.52, 211.95) * mm, "end": v(-30.14, 211.95) * mm});
            skLineSegment(sketch, "E53.1", {"start": v(-30.14, 211.95) * mm, "end": v(-27.45, 207.29) * mm});
            skLineSegment(sketch, "E53.2", {"start": v(-27.45, 207.29) * mm, "end": v(-30.14, 202.63) * mm});
            skLineSegment(sketch, "E53.3", {"start": v(-30.14, 202.63) * mm, "end": v(-35.52, 202.63) * mm});
            skLineSegment(sketch, "E53.4", {"start": v(-35.52, 202.63) * mm, "end": v(-38.2, 207.29) * mm});
            skLineSegment(sketch, "E53.5", {"start": v(-38.2, 207.29) * mm, "end": v(-35.52, 211.95) * mm});
            skPoint(sketch, "E53.0.midPoint", {"position": v(-32.83, 211.95) * mm});
            skCircle(sketch, "E54.0", {"center": v(-64.85, 199.6) * mm, "radius": 6.5 * mm, "construction": true});
            skCircle(sketch, "E55.cCircle", {"center": v(-64.85, 199.6) * mm, "radius": 4.69 * mm, "construction": true});
            skLineSegment(sketch, "E55.0", {"start": v(-67.56, 204.29) * mm, "end": v(-62.15, 204.29) * mm});
            skLineSegment(sketch, "E55.1", {"start": v(-62.15, 204.29) * mm, "end": v(-59.44, 199.6) * mm});
            skLineSegment(sketch, "E55.2", {"start": v(-59.44, 199.6) * mm, "end": v(-62.15, 194.92) * mm});
            skLineSegment(sketch, "E55.3", {"start": v(-62.15, 194.92) * mm, "end": v(-67.56, 194.92) * mm});
            skLineSegment(sketch, "E55.4", {"start": v(-67.56, 194.92) * mm, "end": v(-70.26, 199.6) * mm});
            skLineSegment(sketch, "E55.5", {"start": v(-70.26, 199.6) * mm, "end": v(-67.56, 204.29) * mm});
            skPoint(sketch, "E55.0.midPoint", {"position": v(-64.85, 204.29) * mm});
            skCircle(sketch, "E56.0", {"center": v(32.83, 207.29) * mm, "radius": 6.5 * mm, "construction": true});
            skCircle(sketch, "E57.0", {"center": v(64.85, 199.6) * mm, "radius": 6.5 * mm, "construction": true});
            skCircle(sketch, "E58.cCircle", {"center": v(32.83, 207.29) * mm, "radius": 4.78 * mm, "construction": true});
            skLineSegment(sketch, "E58.0", {"start": v(30.07, 212.07) * mm, "end": v(35.6, 212.07) * mm});
            skLineSegment(sketch, "E58.1", {"start": v(35.6, 212.07) * mm, "end": v(38.35, 207.29) * mm});
            skLineSegment(sketch, "E58.2", {"start": v(38.35, 207.29) * mm, "end": v(35.6, 202.5) * mm});
            skLineSegment(sketch, "E58.3", {"start": v(35.6, 202.5) * mm, "end": v(30.07, 202.5) * mm});
            skLineSegment(sketch, "E58.4", {"start": v(30.07, 202.5) * mm, "end": v(27.3, 207.29) * mm});
            skLineSegment(sketch, "E58.5", {"start": v(27.3, 207.29) * mm, "end": v(30.07, 212.07) * mm});
            skPoint(sketch, "E58.0.midPoint", {"position": v(32.83, 212.07) * mm});
            skCircle(sketch, "E59.cCircle", {"center": v(64.85, 199.6) * mm, "radius": 4.69 * mm, "construction": true});
            skLineSegment(sketch, "E59.0", {"start": v(62.15, 204.29) * mm, "end": v(67.56, 204.29) * mm});
            skLineSegment(sketch, "E59.1", {"start": v(67.56, 204.29) * mm, "end": v(70.26, 199.6) * mm});
            skLineSegment(sketch, "E59.2", {"start": v(70.26, 199.6) * mm, "end": v(67.56, 194.92) * mm});
            skLineSegment(sketch, "E59.3", {"start": v(67.56, 194.92) * mm, "end": v(62.15, 194.92) * mm});
            skLineSegment(sketch, "E59.4", {"start": v(62.15, 194.92) * mm, "end": v(59.44, 199.6) * mm});
            skLineSegment(sketch, "E59.5", {"start": v(59.44, 199.6) * mm, "end": v(62.15, 204.29) * mm});
            skPoint(sketch, "E59.0.midPoint", {"position": v(64.85, 204.29) * mm});
            skSolve(sketch);
        }
        {
            var Q0;
            Q0 = qSketchRegion(id + "F32", true);
            extrude(context, id + "F33", {"entities" : qUnion([Q0]), "operationType" : NewBodyOperationType.REMOVE, "oppositeDirection" : true, "depth" : 5 * mm, "offsetDistance" : 25 * mm});
        }
        {
            var Q0;
            Q0=makeQuery(id+"F30.opExtrude","SWEPT_BODY",BODY,{"disambiguationData":[OSD([sQuery(id+"F29.wireOp",EDGE,"E48")])]});
            var Q1;
            Q1=makeQuery(id+"F30.opExtrude","SWEPT_BODY",BODY,{"disambiguationData":[OSD([sQuery(id+"F29.wireOp",EDGE,"E47")])]});
            var Q2;
            Q2=makeQuery(id+"F30.opExtrude","SWEPT_BODY",BODY,{"disambiguationData":[OSD([sQuery(id+"F29.wireOp",EDGE,"E46")])]});
            var Q3;
            Q3=makeQuery(id+"F30.opExtrude","SWEPT_BODY",BODY,{"disambiguationData":[OSD([sQuery(id+"F29.wireOp",EDGE,"E49")])]});
            var Q4;
            Q4=makeQuery(id+"F30.opExtrude","SWEPT_BODY",BODY,{"disambiguationData":[OSD([sQuery(id+"F29.wireOp",EDGE,"E50")])]});
            var Q5;
            Q5=sQuery(id+"F1.wireOp",EDGE,"E5");
            circularPattern(context, id + "F34", {"entities" : qUnion([Q0, Q1, Q2, Q3, Q4]), "axis" : qUnion([Q5]), "angle" : 360 * degree, "instanceCount" : 6, "equalSpace" : true, "computeTransformsWithoutBuiltin" : true});
        }
    });
